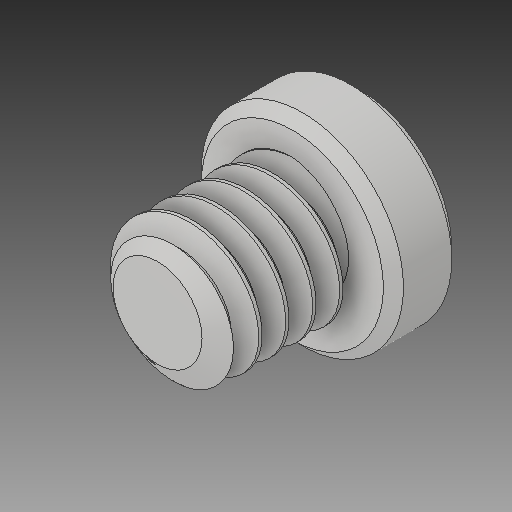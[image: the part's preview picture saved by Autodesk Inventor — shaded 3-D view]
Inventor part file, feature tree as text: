
AUTODESK INVENTOR PART (.ipt)
format: ipt  version: 2019 (Build 230136000, 136)  size: 264,704 bytes
history: mixed  units: in
note: dims shown in document units (in); Inventor stores cm internally (conversion verified against a paired STEP export)
features: chamfer x1, imported_body x1
ambient origin geometry x8: Origin, YZ Plane, XZ Plane, XY Plane, X Axis, Y Axis, Z Axis, Center Point
bodies: Solid1 (imported_parasolid)
feature tree (2):
  chamfer  "Chamfer1"  [1 undecoded]
  imported_body  NMx_Import_Brep_tag  [imported B-rep: ~3 faces, bbox_mm=None]
note: 1 required parameter value undecoded (feature->parameter linkage not recoverable at this tier; creation-order binding heuristic only, values carry confidence <= 0.55)
